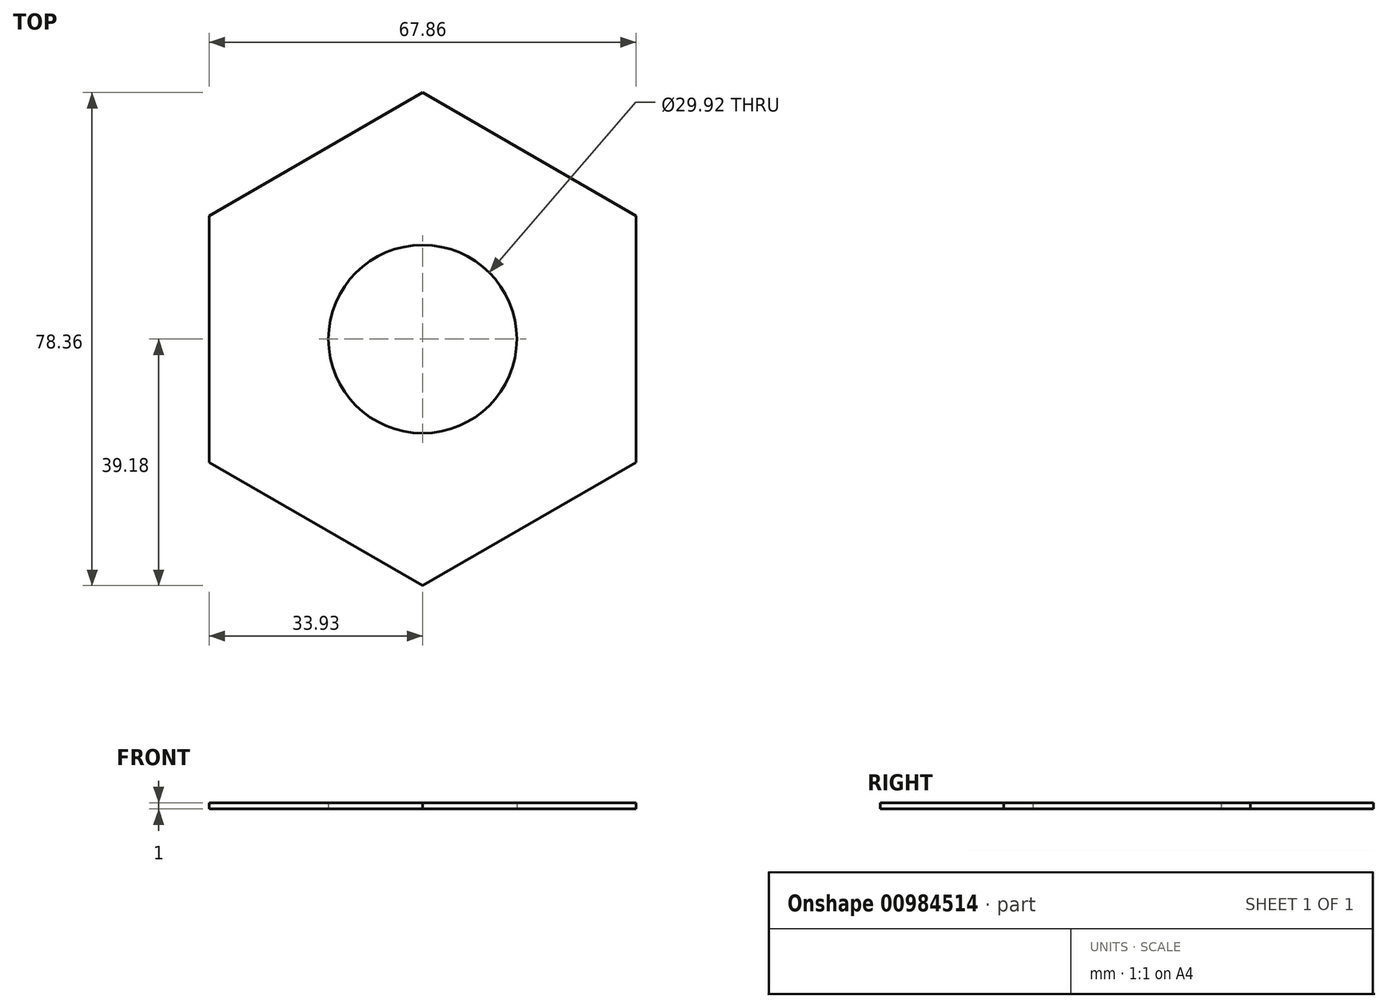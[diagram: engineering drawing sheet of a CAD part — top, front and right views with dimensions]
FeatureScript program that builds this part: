
annotation { "Feature Type Name" : "Feature", "Feature Type Description" : "" }
export const myFeature = defineFeature(function(context is Context, id is Id, definition is map)
    precondition{}
    {
        {
            var Q0;
            Q0=qCreatedBy(makeId("Top.planeOp"),FACE);
            var sketch = newSketch(context, id + "F0", { "sketchPlane" : qUnion([Q0])});
            skCircle(sketch, "E0.cCircle", {"center": v(0, 0) * mm, "radius": 33.93 * mm, "construction": true});
            skLineSegment(sketch, "E0.0", {"start": v(33.93, 19.6) * mm, "end": v(33.93, -19.6) * mm});
            skLineSegment(sketch, "E0.1", {"start": v(33.93, -19.6) * mm, "end": v(0, -39.18) * mm});
            skLineSegment(sketch, "E0.2", {"start": v(0, -39.18) * mm, "end": v(-33.93, -19.6) * mm});
            skLineSegment(sketch, "E0.3", {"start": v(-33.93, -19.6) * mm, "end": v(-33.93, 19.6) * mm});
            skLineSegment(sketch, "E0.4", {"start": v(-33.93, 19.6) * mm, "end": v(0, 39.18) * mm});
            skLineSegment(sketch, "E0.5", {"start": v(0, 39.18) * mm, "end": v(33.93, 19.6) * mm});
            skPoint(sketch, "E0.0.midPoint", {"position": v(33.93, 0) * mm});
            skCircle(sketch, "E1", {"center": v(0, 0) * mm, "radius": 14.96 * mm});
            skSolve(sketch);
        }
        {
            var Q0;
            Q0 = qSketchRegion(id + "F0", true);
            extrude(context, id + "F1", {"entities" : qUnion([Q0]), "depth" : 1 * mm, "offsetDistance" : 25.4 * mm});
        }
    });
